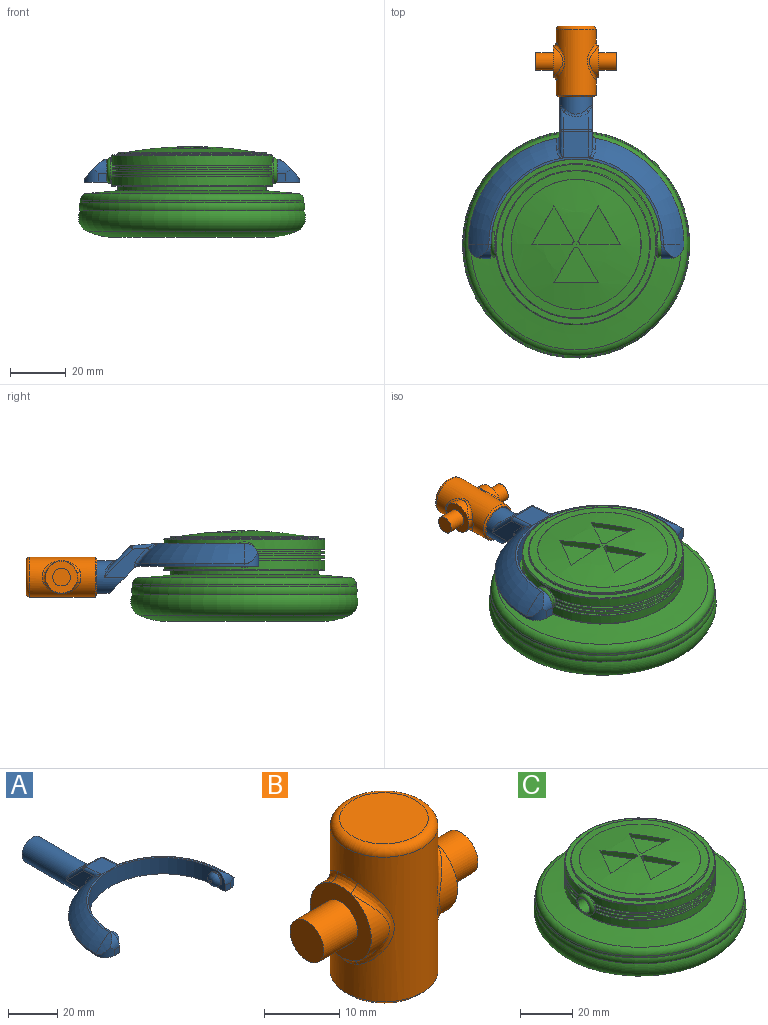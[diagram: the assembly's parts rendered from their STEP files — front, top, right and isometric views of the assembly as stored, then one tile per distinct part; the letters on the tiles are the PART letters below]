
ASSEMBLY  parts=3 mates=2
PART A: 48 faces, bbox 77.3x80.8x18.2 mm
  f0: plane 11.99x9.83mm, normal (0,-0.71,-0.71), area 141.5mm2, adj f1,f2,f9,f30,f43,f46
  f1: plane 15.39x10.49mm, normal (-1,0,0), area 63.5mm2, adj f0,f30,f32,f36,f46,f47
  f2: plane 15.39x10.49mm, normal (1,0,0), area 63.5mm2, adj f0,f30,f34,f39,f43,f44
  f3: plane 9.14x6.37mm, normal (0,0.71,0.71), area 67.6mm2, adj f35,f36,f39,f40
  f4: cylinder r=38.61mm len=37.99mm, axis (0,0,-1), area 42.6mm2, adj f6,f9,f17,f46,f47
  f5: torus R=19.3mm, axis (0,0,-1), area 507.8mm2, adj f10,f11,f12,f29,f42,f44
  f6: torus R=19.3mm, axis (0,0,-1), area 507.8mm2, adj f4,f11,f15,f28,f45,f47
  f7: cylinder r=30.48mm len=60.96mm, axis (0,0,-1), area 746.6mm2, adj f8,f9,f11,f14,f21,f24
  f8: plane 8.13x5.08mm, normal (-1,0,0), area 19.9mm2, adj f7,f9,f13,f19,f24
  f9: plane 77.22x43.73mm, normal (0,0,-1), area 956.2mm2, adj f0,f4,f7,f8,f10,f13,f14,f16
  f10: cylinder r=38.61mm len=37.99mm, axis (0,0,-1), area 42.6mm2, adj f5,f9,f20,f43,f44
  f11: plane 62.55x30.95mm, normal (0,0,1), area 75mm2, adj f5,f6,f7,f18,f19,f27
  f12: cylinder r=22.71mm len=7.33mm, axis (0,1,0), area 24.8mm2, adj f5,f19,f20
  f13: plane 3.05x3.05mm, normal (0,-1,0), area 9.3mm2, adj f8,f9,f19,f20
  f14: plane 8.13x5.08mm, normal (1,0,0), area 19.9mm2, adj f7,f9,f16,f18,f21
  f15: cylinder r=22.71mm len=7.33mm, axis (0,1,0), area 24.8mm2, adj f6,f17,f18
  f16: plane 3.05x3.05mm, normal (0,-1,0), area 9.3mm2, adj f9,f14,f17,f18
  f17: cylinder r=5.08mm len=5.08mm, axis (0,0,-1), area 21.9mm2, adj f4,f9,f15,f16,f18
  f18: cylinder r=5.08mm len=5.08mm, axis (-1,0,0), area 21.9mm2, adj f11,f14,f15,f16,f17
  f19: cylinder r=5.08mm len=5.08mm, axis (-1,0,0), area 21.9mm2, adj f8,f11,f12,f13,f20
  f20: cylinder r=5.08mm len=5.08mm, axis (0,0,-1), area 21.9mm2, adj f9,f10,f12,f13,f19
  f21: cylinder r=3.17mm len=6.35mm, axis (-1,0,0), area 12.7mm2, adj f7,f14,f23
  f22: plane 1.27x1.27mm, normal (1,0,0), area 1.3mm2, adj f23
  f23: torus R=0.64mm, axis (1,0,0), area 56.5mm2, adj f21,f22
  f24: cylinder r=3.17mm len=6.35mm, axis (1,0,0), area 12.7mm2, adj f7,f8,f26
  f25: plane 1.27x1.27mm, normal (-1,0,0), area 1.3mm2, adj f26
  f26: torus R=0.64mm, axis (-1,0,0), area 56.5mm2, adj f24,f25
  f27: plane 9.86x9.36mm, normal (0,0.09,1), area 85.6mm2, adj f11,f28,f29,f32,f34,f35,f42,f45
  f28: plane 1.04x0.17mm, normal (0,-1,0), area 0mm2, adj f6,f27,f45
  f29: plane 1.04x0.17mm, normal (0,-1,0), area 0mm2, adj f5,f27,f42
  f30: cylinder r=5.84mm len=33.01mm, axis (0,-1,0), area 1029.7mm2, adj f0,f1,f2,f31,f38,f40,f41
  f31: plane 11.68x11.68mm, normal (0,1,0), area 107.2mm2, adj f30
  f32: cylinder r=1.27mm len=9.13mm, axis (0,-1,0.09), area 14.4mm2, adj f1,f27,f33,f45
  f33: sphere r=1.27mm, area 1.5mm2, adj f32,f35,f36
  f34: cylinder r=1.27mm len=9.13mm, axis (0,1,-0.09), area 14.4mm2, adj f2,f27,f37,f42
  f35: cylinder r=1.27mm len=9.14mm, axis (-1,0,0), area 8.1mm2, adj f3,f27,f33,f37
  f36: cylinder r=1.27mm len=10.91mm, axis (0,-0.71,0.71), area 23.1mm2, adj f1,f3,f33,f38
  f37: sphere r=1.27mm, area 1.5mm2, adj f34,f35,f39
  f38: bspline ~4.55x2.75mm, area 2.3mm2, adj f30,f36,f40
  f39: cylinder r=1.27mm len=10.91mm, axis (0,0.71,-0.71), area 23.1mm2, adj f2,f3,f37,f41
  f40: bspline ~9.14x2.56mm, area 10.7mm2, adj f3,f30,f38,f41
  f41: bspline ~5.23x3.53mm, area 2.3mm2, adj f30,f39,f40
  f42: bspline ~4.62x3.14mm, area 5.2mm2, adj f5,f27,f29,f34,f44
  f43: cylinder r=1.27mm len=1.74mm, axis (0,0,-1), area 1.9mm2, adj f0,f2,f9,f10,f44
  f44: bspline ~8.6x7.86mm, area 11.9mm2, adj f2,f5,f10,f42,f43
  f45: bspline ~4.62x3.14mm, area 5.2mm2, adj f6,f27,f28,f32,f47
  f46: cylinder r=1.27mm len=1.74mm, axis (0,0,-1), area 1.9mm2, adj f0,f1,f4,f9,f47
  f47: bspline ~8.6x7.86mm, area 11.9mm2, adj f1,f4,f6,f45,f46
PART B: 25 faces, bbox 28.9x15.5x25.4 mm
  f0: cylinder r=5.71mm len=10.81mm, axis (-1,0,0), area 26.2mm2, adj f5,f15
  f1: cylinder r=5.71mm len=10.81mm, axis (-1,0,0), area 26.2mm2, adj f8,f11
  f2: cylinder r=7.14mm len=23.5mm, axis (0,0,-1), area 763.2mm2, adj f9,f10,f11,f12,f13,f14,f15,f16
  f3: plane 11.75x11.75mm, normal (0,0,1), area 108.4mm2, adj f17
  f4: plane 13.02x13.02mm, normal (0,0,-1), area 16.3mm2, adj f22,f24
  f5: plane 11.46x11.46mm, normal (1,0,0), area 70.9mm2, adj f0,f6,f13,f16,f18
  f6: cylinder r=5.71mm len=10.81mm, axis (-1,0,0), area 26.2mm2, adj f5,f14
  f7: cylinder r=5.71mm len=10.81mm, axis (-1,0,0), area 26.2mm2, adj f8,f10
  f8: plane 11.46x11.46mm, normal (-1,0,0), area 70.9mm2, adj f1,f7,f9,f12,f20
  f9: bspline ~4.64x1.73mm, area 6.5mm2, adj f2,f8,f10,f11
  f10: bspline ~13.62x4.91mm, area 20.7mm2, adj f2,f7,f9,f12
  f11: bspline ~13.6x4.87mm, area 20.7mm2, adj f1,f2,f9,f12
  f12: bspline ~4.64x1.73mm, area 6.5mm2, adj f2,f8,f10,f11
  f13: bspline ~4.64x1.73mm, area 6.5mm2, adj f2,f5,f14,f15
  f14: bspline ~13.62x4.91mm, area 20.7mm2, adj f2,f6,f13,f16
  f15: bspline ~13.6x4.87mm, area 20.7mm2, adj f0,f2,f13,f16
  f16: bspline ~4.64x1.73mm, area 6.5mm2, adj f2,f5,f14,f15
  f17: torus R=5.87mm, axis (0,0,1), area 83.8mm2, adj f2,f3
  f18: cylinder r=3.17mm len=6.35mm, axis (-1,0,0), area 126.7mm2, adj f5,f19
  f19: plane 6.35x6.35mm, normal (1,0,0), area 31.7mm2, adj f18
  f20: cylinder r=3.17mm len=6.35mm, axis (1,0,0), area 126.7mm2, adj f8,f21
  f21: plane 6.35x6.35mm, normal (-1,0,0), area 31.7mm2, adj f20
  f22: cylinder r=6.1mm len=22.86mm, axis (0,0,-1), area 875.6mm2, adj f4,f23
  f23: plane 12.19x12.19mm, normal (0,0,-1), area 116.7mm2, adj f22
  f24: cone r=7.14mm half-angle=45deg, axis (0,0,1), area 38.5mm2, adj f2,f4
PART C: 64 faces, bbox 96.2x96.2x32.5 mm
  f0: cylinder r=28.87mm len=57.73mm, axis (0,0,-1), area 594.2mm2, adj f1,f2,f54,f55,f60
  f1: plane 57.13x24.72mm, normal (0,0,1), area 102.1mm2, adj f0,f3,f54,f55
  f2: plane 57.13x24.72mm, normal (0,0,1), area 102.1mm2, adj f0,f4,f54,f55
  f3: cylinder r=27.6mm len=54.57mm, axis (0,0,-1), area 50.3mm2, adj f1,f6,f54,f55
  f4: cylinder r=27.6mm len=54.57mm, axis (0,0,-1), area 50.3mm2, adj f2,f5,f54,f55
  f5: plane 57.06x24.48mm, normal (0,0,-1), area 101.4mm2, adj f4,f8,f54,f55
  f6: plane 57.06x24.48mm, normal (0,0,-1), area 101.4mm2, adj f3,f7,f54,f55
  f7: cylinder r=28.87mm len=57.06mm, axis (0,0,-1), area 77.5mm2, adj f6,f9,f54,f55
  f8: cylinder r=28.87mm len=57.06mm, axis (0,0,-1), area 77.5mm2, adj f5,f10,f54,f55
  f9: plane 57.01x24.31mm, normal (0,0,1), area 101mm2, adj f7,f11,f54,f55
  f10: plane 57.01x24.31mm, normal (0,0,1), area 101mm2, adj f8,f12,f54,f55
  f11: cylinder r=27.6mm len=54.44mm, axis (0,0,-1), area 49.5mm2, adj f9,f14,f54,f55
  f12: cylinder r=27.6mm len=54.44mm, axis (0,0,-1), area 49.5mm2, adj f10,f13,f54,f55
  f13: plane 57.01x24.31mm, normal (0,0,-1), area 101mm2, adj f12,f16,f54,f55
  f14: plane 57.01x24.31mm, normal (0,0,-1), area 101mm2, adj f11,f15,f54,f55
  f15: cylinder r=28.87mm len=57.06mm, axis (0,0,-1), area 77.8mm2, adj f14,f22,f54,f55
  f16: cylinder r=28.87mm len=57.06mm, axis (0,0,-1), area 77.8mm2, adj f13,f21,f54,f55
  f17: cylinder r=27.6mm len=54.56mm, axis (0,0,-1), area 49.3mm2, adj f19,f22,f54,f55
  f18: cylinder r=27.6mm len=54.56mm, axis (0,0,-1), area 49.3mm2, adj f20,f21,f54,f55
  f19: plane 57.13x24.71mm, normal (0,0,-1), area 102mm2, adj f17,f23,f54,f55
  f20: plane 57.13x24.71mm, normal (0,0,-1), area 102mm2, adj f18,f23,f54,f55
  f21: plane 57.06x24.48mm, normal (0,0,1), area 101.4mm2, adj f16,f18,f54,f55
  f22: plane 57.06x24.48mm, normal (0,0,1), area 101.4mm2, adj f15,f17,f54,f55
  f23: cylinder r=28.87mm len=57.73mm, axis (0,0,-1), area 596.5mm2, adj f19,f20,f54,f55,f61
  f24: sphere r=135.39mm, area 1385.3mm2, adj f38,f39,f40,f41,f43,f44,f45,f46
  f25: plane 39.33x39.33mm, normal (0,0,-1), area 1214.6mm2, adj f26
  f26: torus R=20.12mm, axis (0,0,-1), area 1429.3mm2, adj f25,f27
  f27: torus R=27.74mm, axis (0,0,-1), area 3542.1mm2, adj f26,f28
  f28: torus R=35.36mm, axis (0,0,-1), area 2180.1mm2, adj f27,f29
  f29: torus R=37.35mm, axis (0,0,-1), area 734.6mm2, adj f28,f30
  f30: cylinder r=40.06mm len=80.11mm, axis (0,0,-1), area 213.3mm2, adj f29,f34
  f31: cone r=26.57mm half-angle=85deg, axis (0,0,-1), area 2265mm2, adj f32,f34
  f32: cylinder r=26.57mm len=53.14mm, axis (0,0,-1), area 265mm2, adj f31,f33
  f33: plane 57.23x57.23mm, normal (0,0,-1), area 354.5mm2, adj f32,f60
  f34: torus R=37.52mm, axis (0,0,1), area 928.6mm2, adj f30,f31
  f35: cone r=26.57mm half-angle=87deg, axis (0,0,-1), area 475.4mm2, adj f62,f63
  f36: cylinder r=26.57mm len=53.14mm, axis (0,0,-1), area 92.3mm2, adj f37,f62
  f37: plane 57.23x57.23mm, normal (0,0,1), area 354.5mm2, adj f36,f61
  f38: cylinder r=1.27mm len=2.53mm, axis (0,0,1), area 3.4mm2, adj f24,f39,f41,f42
  f39: plane 14.61x2.53mm, normal (0,1,0), area 32.2mm2, adj f24,f38,f40,f42
  f40: plane 13.75x7.94mm, normal (-0.87,-0.5,0), area 28mm2, adj f24,f39,f41,f42
  f41: plane 12.65x7.3mm, normal (0.87,-0.5,0), area 32.2mm2, adj f24,f38,f40,f42
  f42: plane 15.24x13.75mm, normal (0,0,1), area 108.3mm2, adj f38,f39,f40,f41
  f43: cylinder r=1.27mm len=2.53mm, axis (0,0,1), area 3.4mm2, adj f24,f44,f46,f47
  f44: plane 12.65x7.3mm, normal (0.87,-0.5,0), area 32.2mm2, adj f24,f43,f45,f47
  f45: plane 15.88x1.84mm, normal (0,1,0), area 28mm2, adj f24,f44,f46,f47
  f46: plane 12.65x7.3mm, normal (-0.87,-0.5,0), area 32.2mm2, adj f24,f43,f45,f47
  f47: plane 15.88x12.65mm, normal (0,0,1), area 108.3mm2, adj f43,f44,f45,f46
  f48: cylinder r=1.27mm len=2.53mm, axis (0,0,1), area 3.4mm2, adj f24,f49,f51,f52
  f49: plane 12.65x7.3mm, normal (-0.87,-0.5,0), area 32.2mm2, adj f24,f48,f50,f52
  f50: plane 13.75x7.94mm, normal (0.87,-0.5,0), area 28mm2, adj f24,f49,f51,f52
  f51: plane 14.61x2.53mm, normal (0,1,0), area 32.2mm2, adj f24,f48,f50,f52
  f52: plane 15.24x13.75mm, normal (0,0,1), area 108.3mm2, adj f48,f49,f50,f51
  f53: plane 6.6x6.6mm, normal (1,0,0), area 2.6mm2, adj f58,f59
  f54: cylinder r=4.57mm len=9.14mm, axis (-1,0,0), area 20.2mm2, adj f0,f1,f2,f3,f4,f5,f6,f7
  f55: cylinder r=4.57mm len=9.14mm, axis (-1,0,0), area 20.2mm2, adj f0,f1,f2,f3,f4,f5,f6,f7
  f56: plane 6.6x6.6mm, normal (-1,0,0), area 2.6mm2, adj f57,f59
  f57: torus R=3.3mm, axis (1,0,0), area 51.5mm2, adj f55,f56
  f58: torus R=3.3mm, axis (1,0,0), area 51.5mm2, adj f53,f54
  f59: cylinder r=3.17mm len=60.96mm, axis (1,0,0), area 1216.1mm2, adj f53,f56
  f60: torus R=28.61mm, axis (0,0,1), area 72.1mm2, adj f0,f33
  f61: torus R=28.61mm, axis (0,0,-1), area 72.1mm2, adj f23,f37
  f62: torus R=26.31mm, axis (0,0,1), area 64.2mm2, adj f35,f36
  f63: torus R=23.29mm, axis (0,0,1), area 4.5mm2, adj f24,f35
PLACE A t=(32.34,27.52,20.85)mm
PLACE B rot(axis=(-1,0,0),90deg) t=(32.34,80.3,16.88)mm
PLACE C t=(32.34,27.52,33.52)mm
MATE revolute A.f24 <-> C.f54  axis (-1,0,0) through (62.82,27.52,24.92)mm
MATE revolute B.f2 <-> A.f30  axis (0,-1,0) through (32.34,103.16,16.88)mm
